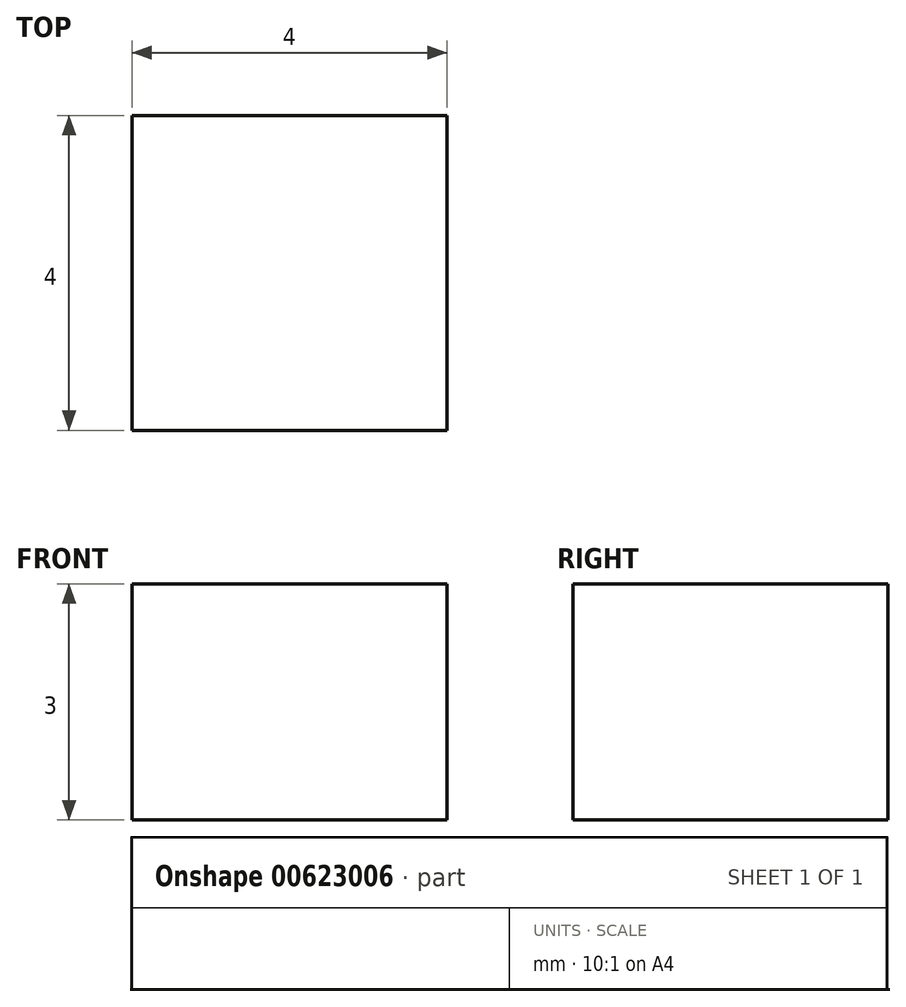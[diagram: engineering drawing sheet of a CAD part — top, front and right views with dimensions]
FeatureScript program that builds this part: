
annotation { "Feature Type Name" : "Feature", "Feature Type Description" : "" }
export const myFeature = defineFeature(function(context is Context, id is Id, definition is map)
    precondition{}
    {
        {
            var Q0;
            Q0=qCreatedBy(makeId("Front.planeOp"),FACE);
            var sketch = newSketch(context, id + "F0", { "sketchPlane" : qUnion([Q0])});
            skLineSegment(sketch, "E0.bottom", {"start": v(0, 0) * mm, "end": v(-300, 0) * mm});
            skLineSegment(sketch, "E0.top", {"start": v(0, 19) * mm, "end": v(-300, 19) * mm});
            skLineSegment(sketch, "E0.left", {"start": v(0, 0) * mm, "end": v(0, 19) * mm});
            skLineSegment(sketch, "E0.right", {"start": v(-300, 0) * mm, "end": v(-300, 19) * mm});
            skLineSegment(sketch, "E1.bottom", {"start": v(-300, 0) * mm, "end": v(-280, 0) * mm});
            skLineSegment(sketch, "E2.bottom", {"start": v(-260, 0) * mm, "end": v(-240, 0) * mm});
            skLineSegment(sketch, "E2.top", {"start": v(-260, 4) * mm, "end": v(-240, 4) * mm});
            skLineSegment(sketch, "E2.left", {"start": v(-260, 0) * mm, "end": v(-260, 4) * mm});
            skLineSegment(sketch, "E2.right", {"start": v(-240, 0) * mm, "end": v(-240, 4) * mm});
            skLineSegment(sketch, "E3.bottom", {"start": v(-80, 0) * mm, "end": v(-100, 0) * mm});
            skLineSegment(sketch, "E3.top", {"start": v(-80, 4) * mm, "end": v(-100, 4) * mm});
            skLineSegment(sketch, "E3.left", {"start": v(-80, 0) * mm, "end": v(-80, 4) * mm});
            skLineSegment(sketch, "E3.right", {"start": v(-100, 0) * mm, "end": v(-100, 4) * mm});
            skLineSegment(sketch, "E4.bottom", {"start": v(-120, 0) * mm, "end": v(-140, 0) * mm});
            skLineSegment(sketch, "E4.top", {"start": v(-120, 4) * mm, "end": v(-140, 4) * mm});
            skLineSegment(sketch, "E4.left", {"start": v(-120, 0) * mm, "end": v(-120, 4) * mm});
            skLineSegment(sketch, "E4.right", {"start": v(-140, 0) * mm, "end": v(-140, 4) * mm});
            skLineSegment(sketch, "E5.bottom", {"start": v(-160, 0) * mm, "end": v(-180, 0) * mm});
            skLineSegment(sketch, "E5.top", {"start": v(-160, 4) * mm, "end": v(-180, 4) * mm});
            skLineSegment(sketch, "E5.left", {"start": v(-160, 0) * mm, "end": v(-160, 4) * mm});
            skLineSegment(sketch, "E5.right", {"start": v(-180, 0) * mm, "end": v(-180, 4) * mm});
            skLineSegment(sketch, "E6.bottom", {"start": v(-200, 0) * mm, "end": v(-220, 0) * mm});
            skLineSegment(sketch, "E6.top", {"start": v(-200, 4) * mm, "end": v(-220, 4) * mm});
            skLineSegment(sketch, "E6.left", {"start": v(-200, 0) * mm, "end": v(-200, 4) * mm});
            skLineSegment(sketch, "E6.right", {"start": v(-220, 0) * mm, "end": v(-220, 4) * mm});
            skLineSegment(sketch, "E7.bottom", {"start": v(-40, 0) * mm, "end": v(-60, 0) * mm});
            skLineSegment(sketch, "E7.top", {"start": v(-40, 4) * mm, "end": v(-60, 4) * mm});
            skLineSegment(sketch, "E7.left", {"start": v(-40, 0) * mm, "end": v(-40, 4) * mm});
            skLineSegment(sketch, "E7.right", {"start": v(-60, 0) * mm, "end": v(-60, 4) * mm});
            skLineSegment(sketch, "E8.bottom", {"start": v(-300, 0) * mm, "end": v(-296, 0) * mm});
            skLineSegment(sketch, "E8.top", {"start": v(-300, 0) * mm, "end": v(-296, 0) * mm});
            skLineSegment(sketch, "E8.left", {"start": v(-300, 0) * mm, "end": v(-300, 0) * mm});
            skLineSegment(sketch, "E8.right", {"start": v(-296, 0) * mm, "end": v(-296, 0) * mm});
            skPoint(sketch, "E9.oppositeSnap0", {"position": v(-296, 0) * mm});
            skLineSegment(sketch, "E10.bottom", {"start": v(0, 0) * mm, "end": v(-4, 0) * mm});
            skLineSegment(sketch, "E10.top", {"start": v(0, 0) * mm, "end": v(-4, 0) * mm});
            skLineSegment(sketch, "E10.left", {"start": v(0, 0) * mm, "end": v(0, 0) * mm});
            skLineSegment(sketch, "E10.right", {"start": v(-4, 0) * mm, "end": v(-4, 0) * mm});
            skLineSegment(sketch, "E11.bottom", {"start": v(0, 19) * mm, "end": v(-4, 19) * mm});
            skLineSegment(sketch, "E11.top", {"start": v(0, 12) * mm, "end": v(-4, 12) * mm});
            skLineSegment(sketch, "E11.left", {"start": v(0, 19) * mm, "end": v(0, 12) * mm});
            skLineSegment(sketch, "E11.right", {"start": v(-4, 19) * mm, "end": v(-4, 12) * mm});
            skPoint(sketch, "E12.oppositeSnap0", {"position": v(-4, 15.5) * mm});
            skLineSegment(sketch, "E12.bottom", {"start": v(0, 19) * mm, "end": v(-20, 19) * mm});
            skLineSegment(sketch, "E12.left", {"start": v(0, 19) * mm, "end": v(0, 16.5) * mm});
            skLineSegment(sketch, "E13.bottom", {"start": v(-80, 19) * mm, "end": v(-100, 19) * mm});
            skLineSegment(sketch, "E13.top", {"start": v(-80, 15) * mm, "end": v(-100, 15) * mm});
            skLineSegment(sketch, "E13.left", {"start": v(-80, 19) * mm, "end": v(-80, 15) * mm});
            skLineSegment(sketch, "E13.right", {"start": v(-100, 19) * mm, "end": v(-100, 15) * mm});
            skPoint(sketch, "E14.firstSnap0", {"position": v(-120, 2) * mm});
            skLineSegment(sketch, "E14.bottom", {"start": v(-120, 19) * mm, "end": v(-140, 19) * mm});
            skLineSegment(sketch, "E14.top", {"start": v(-120, 15) * mm, "end": v(-140, 15) * mm});
            skLineSegment(sketch, "E14.left", {"start": v(-120, 19) * mm, "end": v(-120, 15) * mm});
            skLineSegment(sketch, "E14.right", {"start": v(-140, 19) * mm, "end": v(-140, 15) * mm});
            skLineSegment(sketch, "E15.bottom", {"start": v(-160, 19) * mm, "end": v(-180, 19) * mm});
            skLineSegment(sketch, "E15.top", {"start": v(-160, 15) * mm, "end": v(-180, 15) * mm});
            skLineSegment(sketch, "E15.left", {"start": v(-160, 19) * mm, "end": v(-160, 15) * mm});
            skLineSegment(sketch, "E15.right", {"start": v(-180, 19) * mm, "end": v(-180, 15) * mm});
            skLineSegment(sketch, "E16.bottom", {"start": v(-200, 19) * mm, "end": v(-220, 19) * mm});
            skLineSegment(sketch, "E16.top", {"start": v(-200, 15) * mm, "end": v(-220, 15) * mm});
            skLineSegment(sketch, "E16.left", {"start": v(-200, 19) * mm, "end": v(-200, 15) * mm});
            skLineSegment(sketch, "E16.right", {"start": v(-220, 19) * mm, "end": v(-220, 15) * mm});
            skLineSegment(sketch, "E17.bottom", {"start": v(-240, 19) * mm, "end": v(-260, 19) * mm});
            skLineSegment(sketch, "E17.top", {"start": v(-240, 14.6) * mm, "end": v(-260, 14.6) * mm});
            skLineSegment(sketch, "E17.left", {"start": v(-240, 19) * mm, "end": v(-240, 14.6) * mm});
            skLineSegment(sketch, "E17.right", {"start": v(-260, 19) * mm, "end": v(-260, 14.6) * mm});
            skLineSegment(sketch, "E18.bottom", {"start": v(-280, 19) * mm, "end": v(-300, 19) * mm});
            skLineSegment(sketch, "E19.bottom", {"start": v(-300, 12) * mm, "end": v(-296, 12) * mm});
            skLineSegment(sketch, "E19.top", {"start": v(-300, 19) * mm, "end": v(-296, 19) * mm});
            skLineSegment(sketch, "E19.left", {"start": v(-300, 12) * mm, "end": v(-300, 19) * mm});
            skLineSegment(sketch, "E19.right", {"start": v(-296, 12) * mm, "end": v(-296, 19) * mm});
            skLineSegment(sketch, "E20.bottom", {"start": v(-280, 19) * mm, "end": v(-296, 19) * mm});
            skLineSegment(sketch, "E20.top", {"start": v(-280, 15) * mm, "end": v(-296, 15) * mm});
            skLineSegment(sketch, "E20.left", {"start": v(-280, 19) * mm, "end": v(-280, 15) * mm});
            skLineSegment(sketch, "E20.right", {"start": v(-296, 19) * mm, "end": v(-296, 15) * mm});
            skLineSegment(sketch, "E21.bottom", {"start": v(-280, 0) * mm, "end": v(-296, 0) * mm});
            skLineSegment(sketch, "E21.top", {"start": v(-280, 4) * mm, "end": v(-296, 4) * mm});
            skLineSegment(sketch, "E21.left", {"start": v(-280, 0) * mm, "end": v(-280, 4) * mm});
            skLineSegment(sketch, "E21.right", {"start": v(-296, 0) * mm, "end": v(-296, 4) * mm});
            skLineSegment(sketch, "E22.bottom", {"start": v(-20, 19) * mm, "end": v(-4, 19) * mm});
            skLineSegment(sketch, "E22.top", {"start": v(-20, 15) * mm, "end": v(-4, 15) * mm});
            skLineSegment(sketch, "E22.left", {"start": v(-20, 19) * mm, "end": v(-20, 15) * mm});
            skLineSegment(sketch, "E22.right", {"start": v(-4, 19) * mm, "end": v(-4, 15) * mm});
            skLineSegment(sketch, "E23.bottom", {"start": v(-20, 0) * mm, "end": v(-4, 0) * mm});
            skLineSegment(sketch, "E24.top", {"start": v(-20, 4) * mm, "end": v(-4, 4) * mm});
            skLineSegment(sketch, "E24.left", {"start": v(-20, 0) * mm, "end": v(-20, 4) * mm});
            skLineSegment(sketch, "E24.right", {"start": v(-4, 0) * mm, "end": v(-4, 4) * mm});
            skLineSegment(sketch, "E25.bottom", {"start": v(-40, 19) * mm, "end": v(-60, 19) * mm});
            skLineSegment(sketch, "E25.top", {"start": v(-40, 15) * mm, "end": v(-60, 15) * mm});
            skLineSegment(sketch, "E25.left", {"start": v(-40, 19) * mm, "end": v(-40, 15) * mm});
            skLineSegment(sketch, "E25.right", {"start": v(-60, 19) * mm, "end": v(-60, 15) * mm});
            skLineSegment(sketch, "E26.top", {"start": v(-300, 3) * mm, "end": v(-296, 3) * mm});
            skLineSegment(sketch, "E26.left", {"start": v(-300, 0) * mm, "end": v(-300, 3) * mm});
            skLineSegment(sketch, "E26.right", {"start": v(-296, 0) * mm, "end": v(-296, 3) * mm});
            skLineSegment(sketch, "E27.bottom", {"start": v(-4, 0) * mm, "end": v(0, 0) * mm});
            skLineSegment(sketch, "E27.top", {"start": v(-4, 3) * mm, "end": v(0, 3) * mm});
            skLineSegment(sketch, "E27.left", {"start": v(-4, 0) * mm, "end": v(-4, 3) * mm});
            skLineSegment(sketch, "E27.right", {"start": v(0, 0) * mm, "end": v(0, 3) * mm});
            skSolve(sketch);
        }
        {
            var Q0;
            Q0=makeQuery(id+"F0.imprint","IMPRINT",FACE,{"disambiguationData":[TD([[makeQuery(id+"F0.imprint","IMPRINT",EDGE,{"derivedFrom":sQuery(id+"F0.wireOp",EDGE,"E0.left")}),1.0]])]});
            extrude(context, id + "F1", {"entities" : qUnion([Q0]), "depth" : 4 * mm, "offsetDistance" : 25 * mm});
        }
    });
